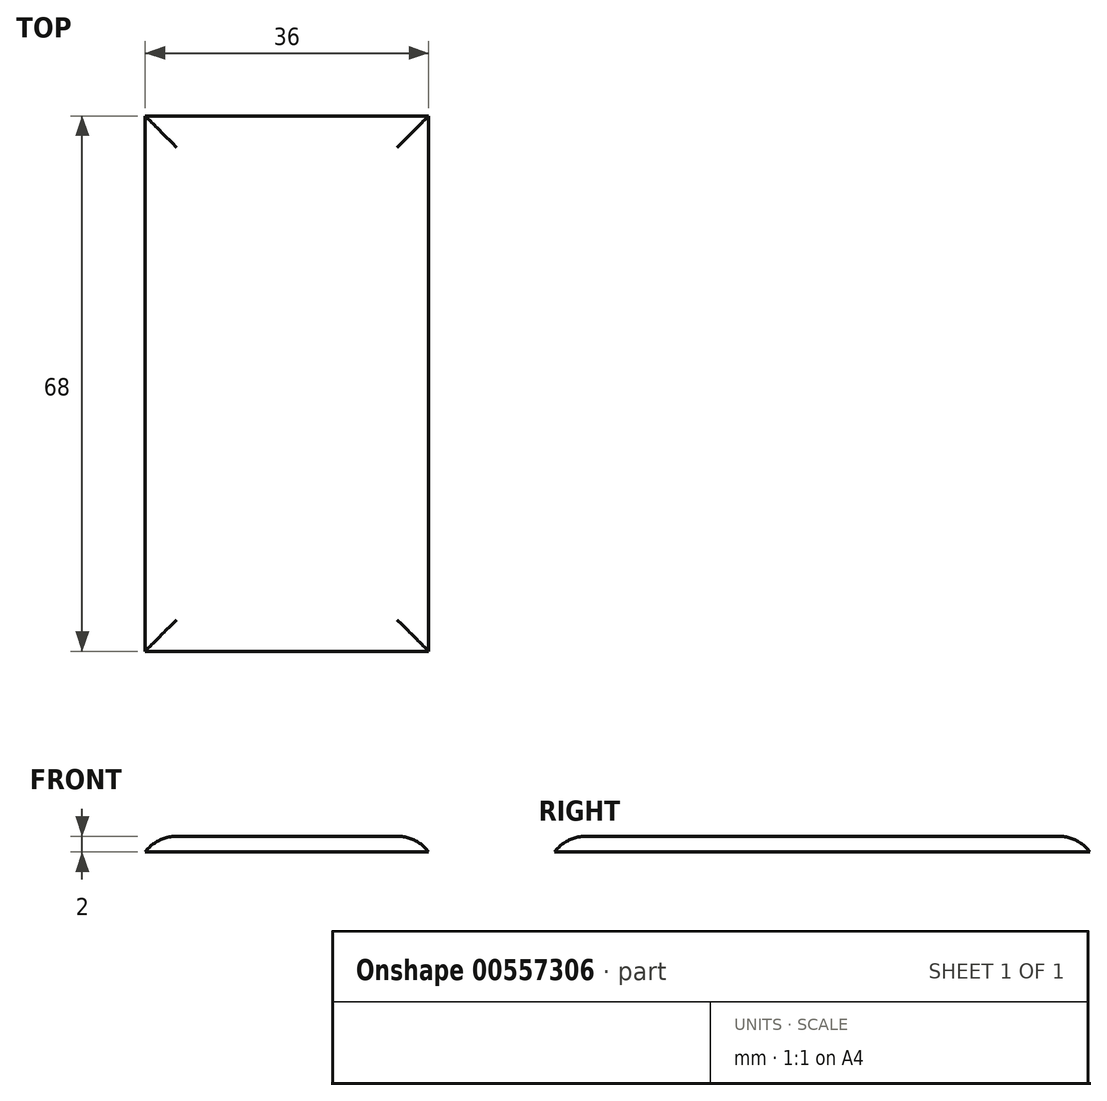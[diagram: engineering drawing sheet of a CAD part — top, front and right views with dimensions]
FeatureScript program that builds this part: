
annotation { "Feature Type Name" : "Feature", "Feature Type Description" : "" }
export const myFeature = defineFeature(function(context is Context, id is Id, definition is map)
    precondition{}
    {
        {
            var Q0;
            Q0=qCreatedBy(makeId("Top.planeOp"),FACE);
            var sketch = newSketch(context, id + "F0", { "sketchPlane" : qUnion([Q0])});
            skLineSegment(sketch, "E0.bottom", {"start": v(0, 0) * mm, "end": v(36, 0) * mm});
            skLineSegment(sketch, "E0.top", {"start": v(0, 68) * mm, "end": v(36, 68) * mm});
            skLineSegment(sketch, "E0.left", {"start": v(0, 0) * mm, "end": v(0, 68) * mm});
            skLineSegment(sketch, "E0.right", {"start": v(36, 0) * mm, "end": v(36, 68) * mm});
            skSolve(sketch);
        }
        {
            var Q0;
            Q0=makeQuery(id+"F0.imprint","IMPRINT",FACE,{"disambiguationData":[TD([[makeQuery(id+"F0.imprint","IMPRINT",EDGE,{"derivedFrom":sQuery(id+"F0.wireOp",EDGE,"E0.bottom")}),1.0]])]});
            extrude(context, id + "F1", {"entities" : qUnion([Q0]), "depth" : 2 * mm, "offsetDistance" : 25 * mm});
        }
        {
            var Q0;
            Q0=makeQuery(id+"F1.opExtrude","CAP_EDGE",EDGE,{"disambiguationData":[OSD([sQuery(id+"F0.wireOp",EDGE,"E0.right")])],"isStart":false});
            var Q1;
            Q1=makeQuery(id+"F1.opExtrude","CAP_EDGE",EDGE,{"disambiguationData":[OSD([sQuery(id+"F0.wireOp",EDGE,"E0.bottom")])],"isStart":false});
            var Q2;
            Q2=makeQuery(id+"F1.opExtrude","CAP_EDGE",EDGE,{"disambiguationData":[OSD([sQuery(id+"F0.wireOp",EDGE,"E0.left")])],"isStart":false});
            var Q3;
            Q3=makeQuery(id+"F1.opExtrude","CAP_EDGE",EDGE,{"disambiguationData":[OSD([sQuery(id+"F0.wireOp",EDGE,"E0.top")])],"isStart":false});
            fillet(context, id + "F2", {"entities" : qUnion([Q0, Q1, Q2, Q3]), "radius" : 5 * mm, "tangentPropagation" : true, "allowEdgeOverflow" : false});
        }
    });
